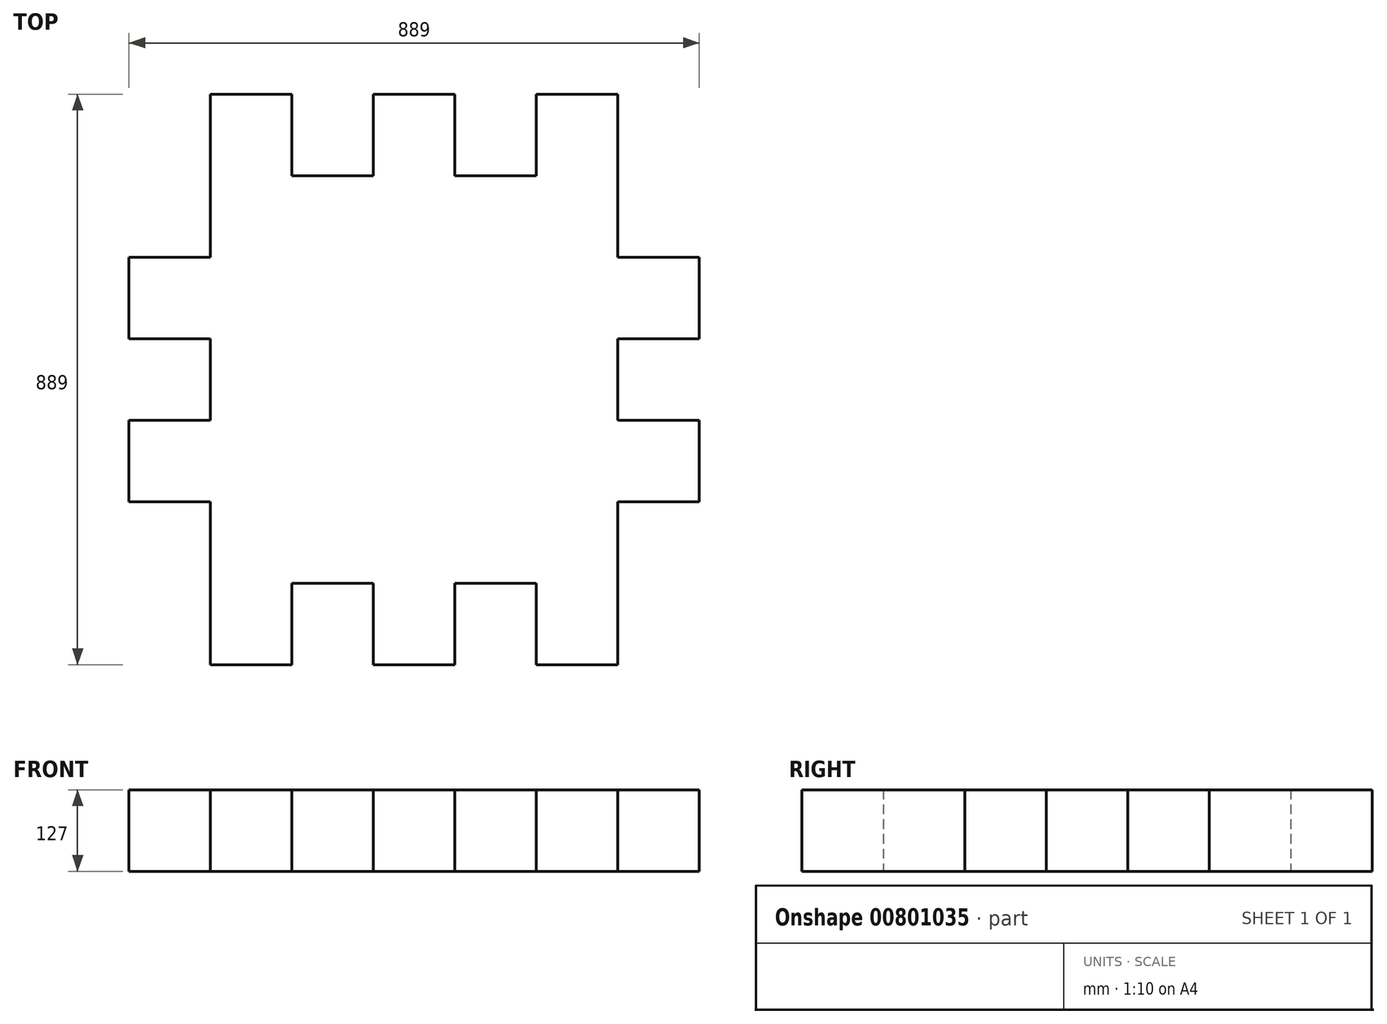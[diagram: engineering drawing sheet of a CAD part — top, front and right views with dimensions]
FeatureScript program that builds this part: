
annotation { "Feature Type Name" : "Feature", "Feature Type Description" : "" }
export const myFeature = defineFeature(function(context is Context, id is Id, definition is map)
    precondition{}
    {
        {
            var Q0;
            Q0=qCreatedBy(makeId("Top.planeOp"),FACE);
            var sketch = newSketch(context, id + "F0", { "sketchPlane" : qUnion([Q0])});
            skLineSegment(sketch, "E0.bottom", {"start": v(0, 0) * mm, "end": v(635, 0) * mm});
            skLineSegment(sketch, "E0.top", {"start": v(0, -635) * mm, "end": v(635, -635) * mm});
            skLineSegment(sketch, "E0.left", {"start": v(0, 0) * mm, "end": v(0, -635) * mm});
            skLineSegment(sketch, "E0.right", {"start": v(635, 0) * mm, "end": v(635, -635) * mm});
            skLineSegment(sketch, "E1.bottom", {"start": v(0, 0) * mm, "end": v(127, 0) * mm});
            skLineSegment(sketch, "E1.top", {"start": v(0, 127) * mm, "end": v(127, 127) * mm});
            skLineSegment(sketch, "E1.left", {"start": v(0, 0) * mm, "end": v(0, 127) * mm});
            skLineSegment(sketch, "E1.right", {"start": v(127, 0) * mm, "end": v(127, 127) * mm});
            skLineSegment(sketch, "E2.bottom", {"start": v(254, 0) * mm, "end": v(381, 0) * mm});
            skLineSegment(sketch, "E2.top", {"start": v(254, 127) * mm, "end": v(381, 127) * mm});
            skLineSegment(sketch, "E2.left", {"start": v(254, 0) * mm, "end": v(254, 127) * mm});
            skLineSegment(sketch, "E2.right", {"start": v(381, 0) * mm, "end": v(381, 127) * mm});
            skLineSegment(sketch, "E3.bottom", {"start": v(635, 0) * mm, "end": v(508, 0) * mm});
            skLineSegment(sketch, "E3.top", {"start": v(635, 127) * mm, "end": v(508, 127) * mm});
            skLineSegment(sketch, "E3.left", {"start": v(635, 0) * mm, "end": v(635, 127) * mm});
            skLineSegment(sketch, "E3.right", {"start": v(508, 0) * mm, "end": v(508, 127) * mm});
            skLineSegment(sketch, "E4.bottom", {"start": v(0, -635) * mm, "end": v(127, -635) * mm});
            skLineSegment(sketch, "E4.top", {"start": v(0, -762) * mm, "end": v(127, -762) * mm});
            skLineSegment(sketch, "E4.left", {"start": v(0, -635) * mm, "end": v(0, -762) * mm});
            skLineSegment(sketch, "E4.right", {"start": v(127, -635) * mm, "end": v(127, -762) * mm});
            skLineSegment(sketch, "E5.bottom", {"start": v(254, -635) * mm, "end": v(381, -635) * mm});
            skLineSegment(sketch, "E5.top", {"start": v(254, -762) * mm, "end": v(381, -762) * mm});
            skLineSegment(sketch, "E5.left", {"start": v(254, -635) * mm, "end": v(254, -762) * mm});
            skLineSegment(sketch, "E5.right", {"start": v(381, -635) * mm, "end": v(381, -762) * mm});
            skLineSegment(sketch, "E6.bottom", {"start": v(635, -635) * mm, "end": v(508, -635) * mm});
            skLineSegment(sketch, "E6.top", {"start": v(635, -762) * mm, "end": v(508, -762) * mm});
            skLineSegment(sketch, "E6.left", {"start": v(635, -635) * mm, "end": v(635, -762) * mm});
            skLineSegment(sketch, "E6.right", {"start": v(508, -635) * mm, "end": v(508, -762) * mm});
            skLineSegment(sketch, "E7.bottom", {"start": v(0, -127) * mm, "end": v(-127, -127) * mm});
            skLineSegment(sketch, "E7.top", {"start": v(0, -254) * mm, "end": v(-127, -254) * mm});
            skLineSegment(sketch, "E7.left", {"start": v(0, -127) * mm, "end": v(0, -254) * mm});
            skLineSegment(sketch, "E7.right", {"start": v(-127, -127) * mm, "end": v(-127, -254) * mm});
            skLineSegment(sketch, "E8.bottom", {"start": v(0, -381) * mm, "end": v(-127, -381) * mm});
            skLineSegment(sketch, "E8.top", {"start": v(0, -508) * mm, "end": v(-127, -508) * mm});
            skLineSegment(sketch, "E8.left", {"start": v(0, -381) * mm, "end": v(0, -508) * mm});
            skLineSegment(sketch, "E8.right", {"start": v(-127, -381) * mm, "end": v(-127, -508) * mm});
            skLineSegment(sketch, "E9.bottom", {"start": v(635, -127) * mm, "end": v(762, -127) * mm});
            skLineSegment(sketch, "E9.top", {"start": v(635, -254) * mm, "end": v(762, -254) * mm});
            skLineSegment(sketch, "E9.left", {"start": v(635, -127) * mm, "end": v(635, -254) * mm});
            skLineSegment(sketch, "E9.right", {"start": v(762, -127) * mm, "end": v(762, -254) * mm});
            skLineSegment(sketch, "E10.bottom", {"start": v(635, -381) * mm, "end": v(762, -381) * mm});
            skLineSegment(sketch, "E10.top", {"start": v(635, -508) * mm, "end": v(762, -508) * mm});
            skLineSegment(sketch, "E10.left", {"start": v(635, -381) * mm, "end": v(635, -508) * mm});
            skLineSegment(sketch, "E10.right", {"start": v(762, -381) * mm, "end": v(762, -508) * mm});
            skSolve(sketch);
        }
        {
            var Q0;
            Q0 = qSketchRegion(id + "F0", true);
            extrude(context, id + "F1", {"entities" : qUnion([Q0]), "depth" : 127 * mm, "offsetDistance" : 25.4 * mm});
        }
    });
